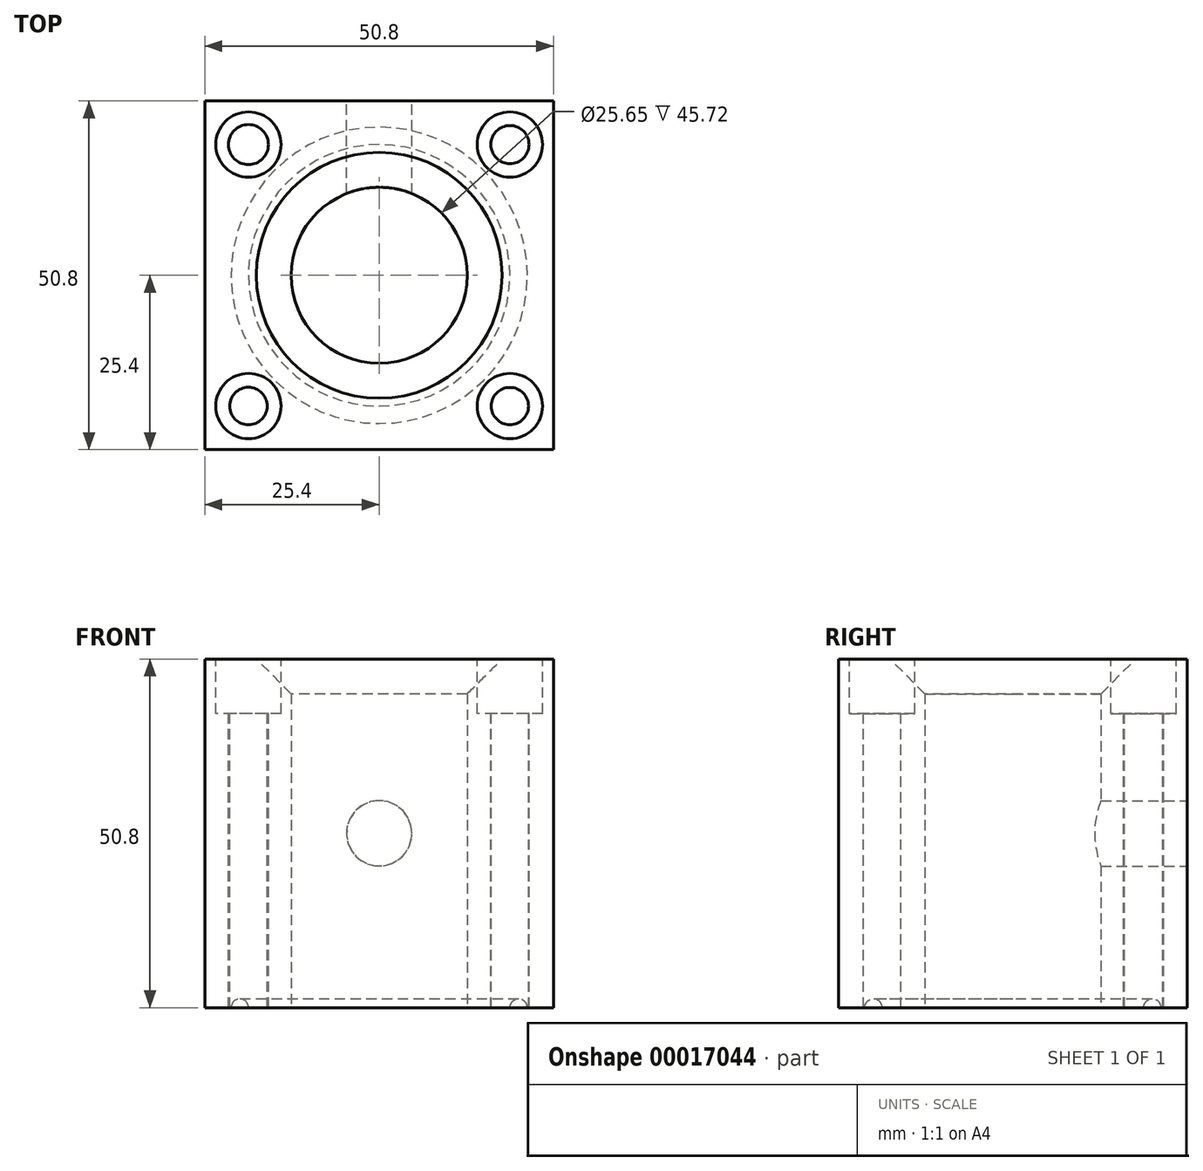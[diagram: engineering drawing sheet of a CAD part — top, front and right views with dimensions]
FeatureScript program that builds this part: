
annotation { "Feature Type Name" : "Feature", "Feature Type Description" : "" }
export const myFeature = defineFeature(function(context is Context, id is Id, definition is map)
    precondition{}
    {
        {
            var Q0;
            Q0=qCreatedBy(makeId("Top.planeOp"),FACE);
            var sketch = newSketch(context, id + "F0", { "sketchPlane" : qUnion([Q0])});
            skCircle(sketch, "E0", {"center": v(0, 0) * mm, "radius": 12.83 * mm});
            skLineSegment(sketch, "E1.bottom", {"start": v(25.4, 25.4) * mm, "end": v(-25.4, 25.4) * mm});
            skLineSegment(sketch, "E1.top", {"start": v(25.4, -25.4) * mm, "end": v(-25.4, -25.4) * mm});
            skLineSegment(sketch, "E1.left", {"start": v(25.4, 25.4) * mm, "end": v(25.4, -25.4) * mm});
            skLineSegment(sketch, "E1.right", {"start": v(-25.4, 25.4) * mm, "end": v(-25.4, -25.4) * mm});
            skSolve(sketch);
        }
        {
            var Q0;
            Q0 = qSketchRegion(id + "F0", true);
            extrude(context, id + "F1", {"entities" : qUnion([Q0]), "depth" : 50.8 * mm});
        }
        {
            var Q0;
            Q0=makeQuery(id+"F1.opExtrude","CAP_FACE",FACE,{"disambiguationData":[OSD([sQuery(id+"F0.wireOp",EDGE,"E0"),sQuery(id+"F0.wireOp",EDGE,"E1.bottom"),sQuery(id+"F0.wireOp",EDGE,"E1.top"),sQuery(id+"F0.wireOp",EDGE,"E1.left"),sQuery(id+"F0.wireOp",EDGE,"E1.right")])],"isStart":true});
            var sketch = newSketch(context, id + "F2", { "sketchPlane" : qUnion([Q0])});
            skCircle(sketch, "E2", {"center": v(0, 0) * mm, "radius": 19.05 * mm});
            skCircle(sketch, "E3", {"center": v(0, 0) * mm, "radius": 21.59 * mm});
            skSolve(sketch);
        }
        {
            var Q0;
            Q0 = qSketchRegion(id + "F2", true);
            extrude(context, id + "F3", {"entities" : qUnion([Q0]), "operationType" : NewBodyOperationType.REMOVE, "oppositeDirection" : true, "depth" : 1.27 * mm});
        }
        {
            var Q0;
            Q0=makeQuery(id+"F3.boolean.opBoolean","COPY",EDGE,{"derivedFrom":makeQuery(id+"F3.opExtrude","CAP_EDGE",EDGE,{"disambiguationData":[OSD([sQuery(id+"F2.wireOp",EDGE,"E2")])],"isStart":false})});
            var Q1;
            Q1=makeQuery(id+"F3.boolean.opBoolean","COPY",EDGE,{"derivedFrom":makeQuery(id+"F3.opExtrude","CAP_EDGE",EDGE,{"disambiguationData":[OSD([sQuery(id+"F2.wireOp",EDGE,"E3")])],"isStart":false})});
            fillet(context, id + "F4", {"entities" : qUnion([Q0, Q1]), "radius" : 1.27 * mm, "tangentPropagation" : true, "allowEdgeOverflow" : false});
        }
        {
            var Q0;
            Q0=makeQuery(id+"F1.opExtrude","CAP_FACE",FACE,{"disambiguationData":[OSD([sQuery(id+"F0.wireOp",EDGE,"E0"),sQuery(id+"F0.wireOp",EDGE,"E1.bottom"),sQuery(id+"F0.wireOp",EDGE,"E1.top"),sQuery(id+"F0.wireOp",EDGE,"E1.left"),sQuery(id+"F0.wireOp",EDGE,"E1.right")])],"isStart":false});
            var sketch = newSketch(context, id + "F5", { "sketchPlane" : qUnion([Q0])});
            skCircle(sketch, "E4", {"center": v(-19.05, 19.05) * mm, "radius": 2.91 * mm});
            skCircle(sketch, "E5", {"center": v(19.05, 19.05) * mm, "radius": 2.78 * mm});
            skCircle(sketch, "E6", {"center": v(19.05, -19.05) * mm, "radius": 2.71 * mm});
            skCircle(sketch, "E7", {"center": v(-19.05, -19.05) * mm, "radius": 2.73 * mm});
            skSolve(sketch);
        }
        {
            var Q0;
            Q0 = qSketchRegion(id + "F5", true);
            extrude(context, id + "F6", {"entities" : qUnion([Q0]), "operationType" : NewBodyOperationType.REMOVE, "endBound" : BoundingType.THROUGH_ALL, "oppositeDirection" : true, "depth" : 25.4 * mm});
        }
        {
            var Q0;
            Q0=makeQuery(id+"F1.opExtrude","CAP_FACE",FACE,{"disambiguationData":[OSD([sQuery(id+"F0.wireOp",EDGE,"E0"),sQuery(id+"F0.wireOp",EDGE,"E1.bottom"),sQuery(id+"F0.wireOp",EDGE,"E1.top"),sQuery(id+"F0.wireOp",EDGE,"E1.left"),sQuery(id+"F0.wireOp",EDGE,"E1.right")])],"isStart":false});
            var sketch = newSketch(context, id + "F7", { "sketchPlane" : qUnion([Q0])});
            skCircle(sketch, "E8", {"center": v(-19.05, 19.05) * mm, "radius": 4.76 * mm});
            skCircle(sketch, "E9", {"center": v(19.05, 19.05) * mm, "radius": 4.76 * mm});
            skCircle(sketch, "E10", {"center": v(19.05, -19.05) * mm, "radius": 4.76 * mm});
            skCircle(sketch, "E11", {"center": v(-19.05, -19.05) * mm, "radius": 4.76 * mm});
            skSolve(sketch);
        }
        {
            var Q0;
            Q0 = qSketchRegion(id + "F7", true);
            extrude(context, id + "F8", {"entities" : qUnion([Q0]), "operationType" : NewBodyOperationType.REMOVE, "oppositeDirection" : true, "depth" : 7.94 * mm});
        }
        {
            var Q0;
            Q0=makeQuery(id+"F1.opExtrude","CAP_EDGE",EDGE,{"disambiguationData":[OSD([sQuery(id+"F0.wireOp",EDGE,"E0")])],"isStart":false});
            chamfer(context, id + "F9", {"entities" : qUnion([Q0]), "width" : 5.08 * mm, "tangentPropagation" : true});
        }
        {
            var Q0;
            Q0=makeQuery(id+"F1.opExtrude","SWEPT_FACE",FACE,{"disambiguationData":[OSD([sQuery(id+"F0.wireOp",EDGE,"E1.bottom")])]});
            var sketch = newSketch(context, id + "F10", { "sketchPlane" : qUnion([Q0])});
            skCircle(sketch, "E12", {"center": v(0, 25.4) * mm, "radius": 4.76 * mm});
            skSolve(sketch);
        }
        {
            var Q0;
            Q0 = qSketchRegion(id + "F10", true);
            extrude(context, id + "F11", {"entities" : qUnion([Q0]), "operationType" : NewBodyOperationType.REMOVE, "oppositeDirection" : true, "depth" : 25.4 * mm});
        }
    });
